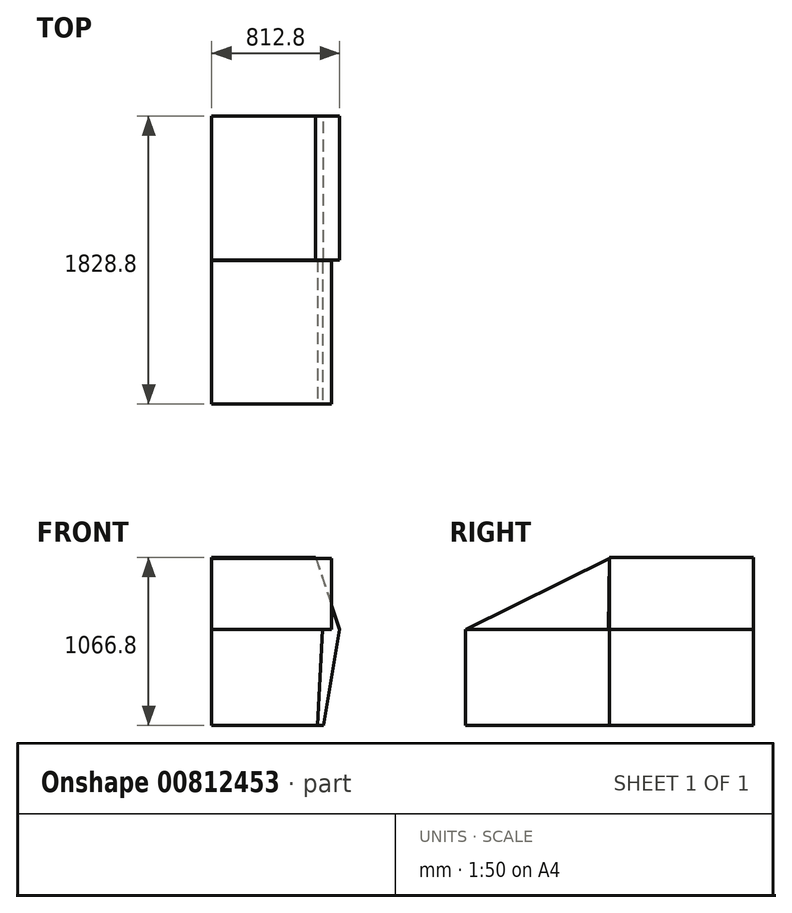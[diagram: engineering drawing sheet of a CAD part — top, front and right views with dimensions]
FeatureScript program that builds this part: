
annotation { "Feature Type Name" : "Feature", "Feature Type Description" : "" }
export const myFeature = defineFeature(function(context is Context, id is Id, definition is map)
    precondition{}
    {
        {
            var Q0;
            Q0=qCreatedBy(makeId("Front.planeOp"),FACE);
            cPlane(context, id + "F0", {"entities" : qUnion([Q0]), "cplaneType" : CPlaneType.OFFSET, "offset" : 304.8 * mm, "width" : 152.4 * mm, "height" : 152.4 * mm});
        }
        {
            var Q0;
            Q0=qCreatedBy(id+"F0.planeOp",FACE);
            cPlane(context, id + "F1", {"entities" : qUnion([Q0]), "cplaneType" : CPlaneType.OFFSET, "offset" : 304.8 * mm, "width" : 152.4 * mm, "height" : 152.4 * mm});
        }
        {
            var Q0;
            Q0=qCreatedBy(id+"F1.planeOp",FACE);
            cPlane(context, id + "F2", {"entities" : qUnion([Q0]), "cplaneType" : CPlaneType.OFFSET, "offset" : 304.8 * mm, "width" : 152.4 * mm, "height" : 152.4 * mm});
        }
        {
            var Q0;
            Q0=qCreatedBy(id+"F2.planeOp",FACE);
            cPlane(context, id + "F3", {"entities" : qUnion([Q0]), "cplaneType" : CPlaneType.OFFSET, "offset" : 304.8 * mm, "width" : 152.4 * mm, "height" : 152.4 * mm});
        }
        {
            var Q0;
            Q0=qCreatedBy(id+"F3.planeOp",FACE);
            cPlane(context, id + "F4", {"entities" : qUnion([Q0]), "cplaneType" : CPlaneType.OFFSET, "offset" : 304.8 * mm, "width" : 152.4 * mm, "height" : 152.4 * mm});
        }
        {
            var Q0;
            Q0=qCreatedBy(id+"F4.planeOp",FACE);
            cPlane(context, id + "F5", {"entities" : qUnion([Q0]), "cplaneType" : CPlaneType.OFFSET, "offset" : 304.8 * mm, "width" : 152.4 * mm, "height" : 152.4 * mm});
        }
        {
            var Q0;
            Q0=qCreatedBy(id+"F5.planeOp",FACE);
            cPlane(context, id + "F6", {"entities" : qUnion([Q0]), "cplaneType" : CPlaneType.OFFSET, "offset" : 304.8 * mm, "width" : 152.4 * mm, "height" : 152.4 * mm});
        }
        {
            var Q0;
            Q0=qCreatedBy(id+"F6.planeOp",FACE);
            cPlane(context, id + "F7", {"entities" : qUnion([Q0]), "cplaneType" : CPlaneType.OFFSET, "offset" : 304.8 * mm, "width" : 152.4 * mm, "height" : 152.4 * mm});
        }
        {
            var Q0;
            Q0=qCreatedBy(id+"F7.planeOp",FACE);
            var sketch = newSketch(context, id + "F8", { "sketchPlane" : qUnion([Q0])});
            skLineSegment(sketch, "E0", {"start": v(703.58, 0) * mm, "end": v(673.1, -609.6) * mm});
            skLineSegment(sketch, "E1", {"start": v(673.1, -609.6) * mm, "end": v(0, -609.6) * mm});
            skLineSegment(sketch, "E2", {"start": v(0, 0) * mm, "end": v(0, -609.6) * mm});
            skLineSegment(sketch, "E3", {"start": v(0, 0) * mm, "end": v(703.58, 0) * mm});
            skPoint(sketch, "E4.orphan", {"position": v(711.2, 0) * mm});
            skPoint(sketch, "E5.end.orphan", {"position": v(711.2, 152.4) * mm});
            skSolve(sketch);
        }
        {
            var Q0;
            Q0=qCreatedBy(id+"F1.planeOp",FACE);
            var sketch = newSketch(context, id + "F9", { "sketchPlane" : qUnion([Q0])});
            skLineSegment(sketch, "E6", {"start": v(0, 0) * mm, "end": v(812.8, 0) * mm});
            skLineSegment(sketch, "E7", {"start": v(812.8, 0) * mm, "end": v(711.2, -609.6) * mm});
            skLineSegment(sketch, "E8", {"start": v(711.2, -609.6) * mm, "end": v(0, -609.6) * mm});
            skLineSegment(sketch, "E9", {"start": v(0, 0) * mm, "end": v(0, -609.6) * mm});
            skLineSegment(sketch, "E10", {"start": v(0, 457.2) * mm, "end": v(660.4, 457.2) * mm});
            skLineSegment(sketch, "E11", {"start": v(660.4, 457.2) * mm, "end": v(812.8, 0) * mm});
            skLineSegment(sketch, "E12", {"start": v(0, 457.2) * mm, "end": v(0, 0) * mm});
            skSolve(sketch);
        }
        {
            var Q0;
            Q0=qCreatedBy(id+"F4.planeOp",FACE);
            var sketch = newSketch(context, id + "F10", { "sketchPlane" : qUnion([Q0])});
            skLineSegment(sketch, "E13", {"start": v(0, 0) * mm, "end": v(673.1, 0) * mm});
            skLineSegment(sketch, "E14", {"start": v(673.1, 0) * mm, "end": v(609.6, -609.6) * mm});
            skLineSegment(sketch, "E15", {"start": v(609.6, -609.6) * mm, "end": v(0, -609.6) * mm});
            skLineSegment(sketch, "E16", {"start": v(0, 0) * mm, "end": v(0, -609.6) * mm});
            skLineSegment(sketch, "E17", {"start": v(0, 457.2) * mm, "end": v(584.2, 457.2) * mm});
            skLineSegment(sketch, "E18", {"start": v(584.2, 457.2) * mm, "end": v(673.1, 0) * mm});
            skLineSegment(sketch, "E19", {"start": v(0, 457.2) * mm, "end": v(0, 0) * mm});
            skSolve(sketch);
        }
        {
            var Q0;
            Q0=qCreatedBy(makeId("Right.planeOp"),FACE);
            var sketch = newSketch(context, id + "F11", { "sketchPlane" : qUnion([Q0])});
            skLineSegment(sketch, "E20", {"start": v(-2437.98, 0) * mm, "end": v(-1526.67, 452.59) * mm});
            skLineSegment(sketch, "E21", {"start": v(-2437.98, 0) * mm, "end": v(-1533.23, 0) * mm});
            skLineSegment(sketch, "E22", {"start": v(-1526.67, 452.59) * mm, "end": v(-1533.23, 0) * mm});
            skSolve(sketch);
        }
        {
            var Q0;
            Q0 = qSketchRegion(id + "F8", true);
            var Q1;
            Q1=qCreatedBy(id+"F4.planeOp",FACE);
            extrude(context, id + "F12", {"entities" : qUnion([Q0]), "endBound" : BoundingType.UP_TO_SURFACE, "oppositeDirection" : true, "depth" : 914.4 * mm, "endBoundEntityFace" : qUnion([Q1]), "offsetDistance" : 25.4 * mm});
        }
        {
            var Q0;
            Q0 = qSketchRegion(id + "F10", true);
            var Q1;
            Q1=qCreatedBy(id+"F1.planeOp",FACE);
            var Q2;
            Q2=sQuery(id+"F9.wireOp",VERTEX,"E7.start");
            extrude(context, id + "F13", {"entities" : qUnion([Q0]), "operationType" : NewBodyOperationType.ADD, "endBound" : BoundingType.UP_TO_VERTEX, "oppositeDirection" : true, "depth" : 25.4 * mm, "endBoundEntityFace" : qUnion([Q1]), "endBoundEntityVertex" : qUnion([Q2]), "offsetDistance" : 25.4 * mm});
        }
        {
            var Q0;
            Q0=makeQuery(id+"F11.imprint","IMPRINT",FACE,{"disambiguationData":[TD([[makeQuery(id+"F11.imprint","IMPRINT",EDGE,{"derivedFrom":sQuery(id+"F11.wireOp",EDGE,"E20")}),-1.0]])]});
            extrude(context, id + "F14", {"entities" : qUnion([Q0]), "operationType" : NewBodyOperationType.ADD, "depth" : 762 * mm, "offsetDistance" : 25.4 * mm});
        }
        {
            var Q0;
            Q0=makeQuery(id+"F9.imprint","IMPRINT",FACE,{"disambiguationData":[TD([[makeQuery(id+"F9.imprint","IMPRINT",EDGE,{"derivedFrom":sQuery(id+"F9.wireOp",EDGE,"E6")}),1.0]])]});
            var Q1;
            Q1=makeQuery(id+"F9.imprint","IMPRINT",FACE,{"disambiguationData":[TD([[makeQuery(id+"F9.imprint","IMPRINT",EDGE,{"derivedFrom":sQuery(id+"F9.wireOp",EDGE,"E6")}),-1.0]])]});
            var Q2;
            Q2=makeQuery(id+"F13.opExtrude","SWEPT_FACE",FACE,{"disambiguationData":[OSD([sQuery(id+"F10.wireOp",EDGE,"E14")])]});
            extrude(context, id + "F15", {"entities" : qUnion([Q0, Q1]), "operationType" : NewBodyOperationType.ADD, "depth" : 914.4 * mm, "endBoundEntityFace" : qUnion([Q2]), "offsetDistance" : 25.4 * mm});
        }
    });
